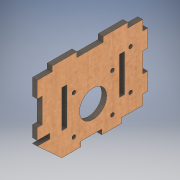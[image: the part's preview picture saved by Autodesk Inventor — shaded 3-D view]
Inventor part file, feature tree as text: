
AUTODESK INVENTOR PART (.ipt)
format: ipt  version: 2019 (Build 230136000, 136)  size: 207,872 bytes
history: native  units: mm
features: sketch x2, other x1, extrude x1, hole x1
ambient origin geometry x8: Origin, YZ Plane, XZ Plane, XY Plane, X Axis, Y Axis, Z Axis, Center Point
bodies: Body1 (feature_tree)
feature tree (5):
  other  "Твердое тело1"
  extrude  "Выдавливание1"  Depth=4.0mm
  hole  "Отверстие1"  [1 undecoded]
  sketch  "Эскиз1"
  sketch  "Эскиз4"
note: 1 required parameter value undecoded (feature->parameter linkage not recoverable at this tier; creation-order binding heuristic only, values carry confidence <= 0.55)
